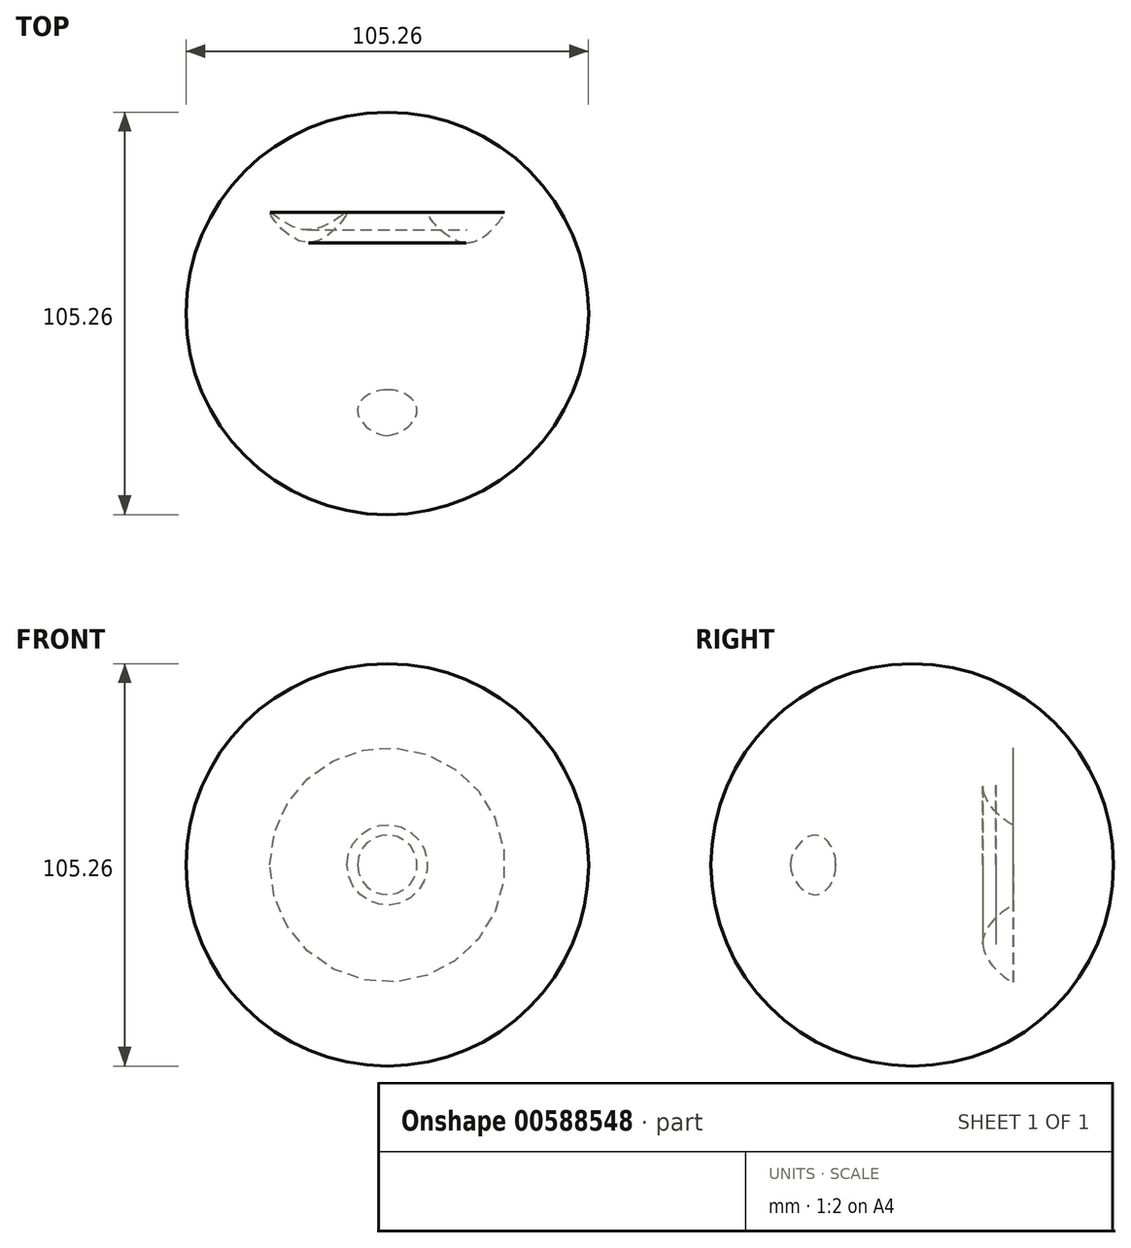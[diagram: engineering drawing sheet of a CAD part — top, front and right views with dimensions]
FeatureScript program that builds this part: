
annotation { "Feature Type Name" : "Feature", "Feature Type Description" : "" }
export const myFeature = defineFeature(function(context is Context, id is Id, definition is map)
    precondition{}
    {
        {
            var Q0;
            Q0=qCreatedBy(makeId("Top.planeOp"),FACE);
            var sketch = newSketch(context, id + "F0", { "sketchPlane" : qUnion([Q0])});
            skCircle(sketch, "E0", {"center": v(0, 0) * mm, "radius": 52.63 * mm});
            skFitSpline(sketch, "E1", {"points": [v(-30.7, 26.42) * mm, v(-20.92, 21.83) * mm, v(-10.54, 26.42) * mm, v(-20.61, 18.48) * mm, v(-30.7, 26.42) * mm]});
            skFitSpline(sketch, "E2.MirrorC", {"points": [v(30.7, 26.42) * mm, v(20.92, 21.83) * mm, v(10.54, 26.42) * mm, v(20.61, 18.48) * mm, v(30.7, 26.42) * mm]});
            skFitSpline(sketch, "E3", {"points": [v(0, -31.91) * mm, v(8.4, -26.11) * mm, v(0, -20) * mm, v(-7.79, -25.2) * mm, v(0, -31.91) * mm]});
            skLineSegment(sketch, "E4", {"start": v(0, 52.63) * mm, "end": v(0, -60) * mm});
            skSolve(sketch);
        }
        {
            var Q0;
            Q0=makeQuery(id+"F0.imprint","IMPRINT",FACE,{"disambiguationData":[TD([[makeQuery(id+"F0.imprint","IMPRINT",EDGE,{"derivedFrom":sQuery(id+"F0.wireOp",EDGE,"E1")}),1.0]])]});
            var Q1;
            Q1=sQuery(id+"F0.wireOp",EDGE,"E4");
            revolve(context, id + "F1", {"entities" : qUnion([Q0]), "axis" : qUnion([Q1]), "revolveType" : RevolveType.FULL});
        }
    });
